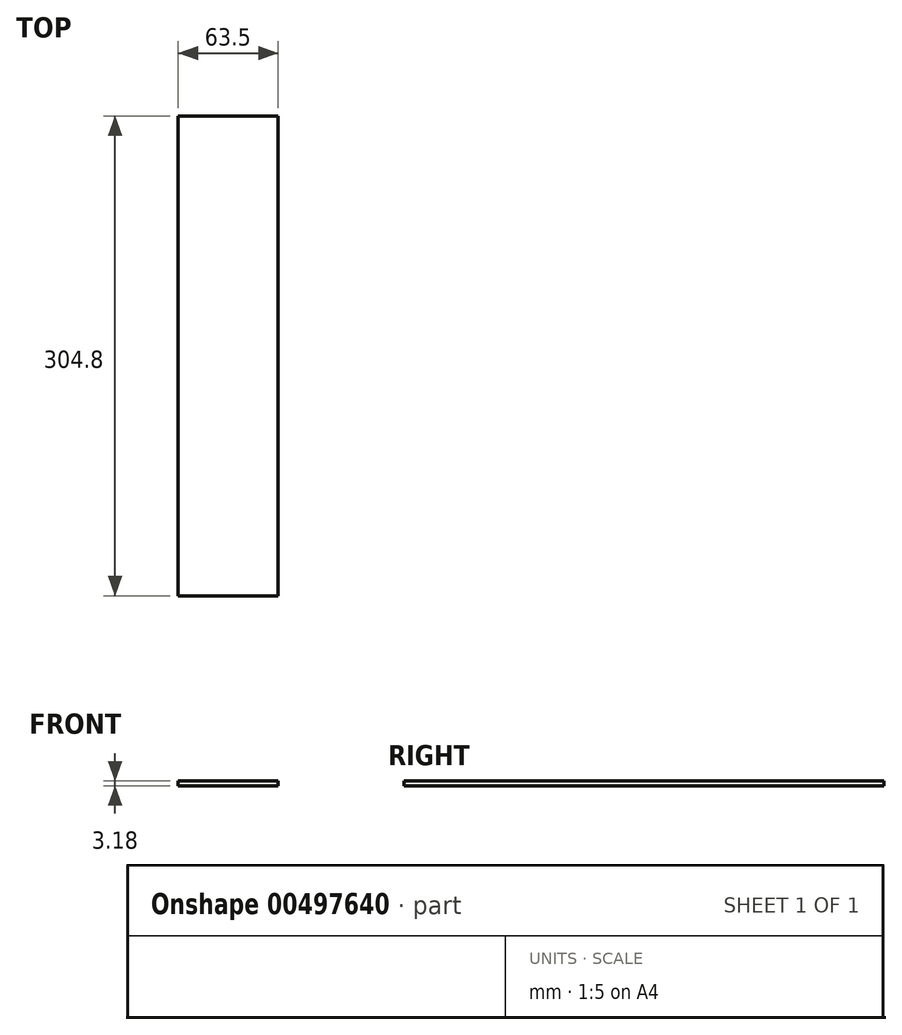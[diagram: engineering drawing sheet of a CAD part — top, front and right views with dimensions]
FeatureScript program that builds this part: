
annotation { "Feature Type Name" : "Feature", "Feature Type Description" : "" }
export const myFeature = defineFeature(function(context is Context, id is Id, definition is map)
    precondition{}
    {
        {
            var Q0;
            Q0=qCreatedBy(makeId("Front.planeOp"),FACE);
            var sketch = newSketch(context, id + "F0", { "sketchPlane" : qUnion([Q0])});
            skLineSegment(sketch, "E0.bottom", {"start": v(31.75, -1.59) * mm, "end": v(-31.75, -1.59) * mm});
            skLineSegment(sketch, "E0.top", {"start": v(31.75, 1.59) * mm, "end": v(-31.75, 1.59) * mm});
            skLineSegment(sketch, "E0.left", {"start": v(31.75, -1.59) * mm, "end": v(31.75, 1.59) * mm});
            skLineSegment(sketch, "E0.right", {"start": v(-31.75, -1.59) * mm, "end": v(-31.75, 1.59) * mm});
            skPoint(sketch, "E0.middle", {"position": v(0, 0) * mm});
            skSolve(sketch);
        }
        {
            var Q0;
            Q0 = qSketchRegion(id + "F0", true);
            extrude(context, id + "F1", {"entities" : qUnion([Q0]), "endBound" : BoundingType.SYMMETRIC, "depth" : 304.8 * mm});
        }
    });
